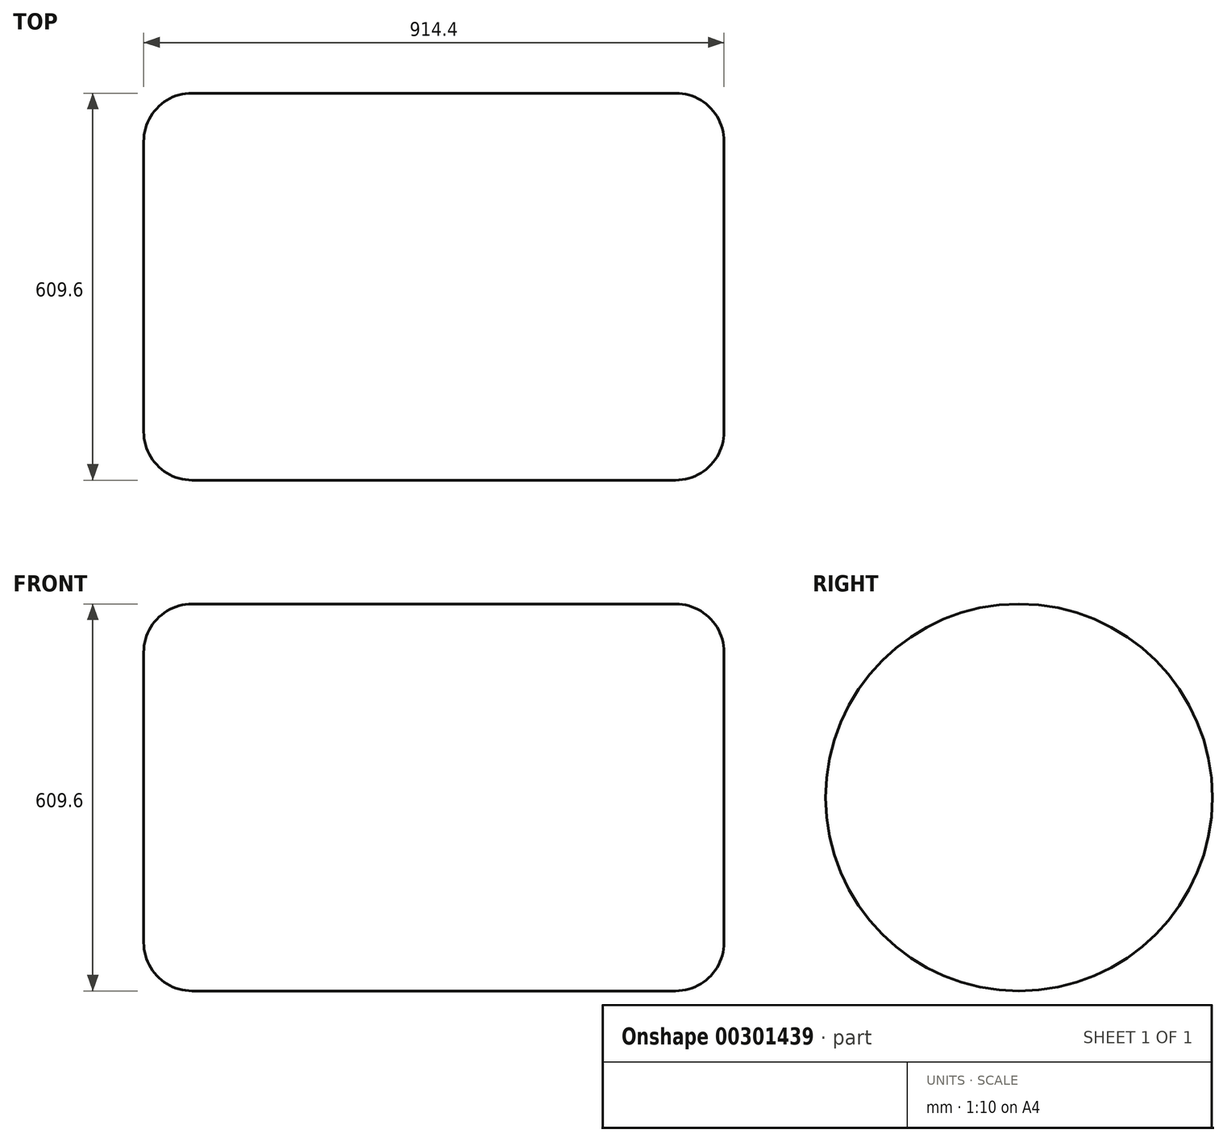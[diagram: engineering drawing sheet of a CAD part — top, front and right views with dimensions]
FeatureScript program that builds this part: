
annotation { "Feature Type Name" : "Feature", "Feature Type Description" : "" }
export const myFeature = defineFeature(function(context is Context, id is Id, definition is map)
    precondition{}
    {
        {
            var Q0;
            Q0=qCreatedBy(makeId("Right.planeOp"),FACE);
            var sketch = newSketch(context, id + "F0", { "sketchPlane" : qUnion([Q0])});
            skCircle(sketch, "E0", {"center": v(0, 0) * mm, "radius": 304.8 * mm});
            skSolve(sketch);
        }
        {
            var Q0;
            Q0=makeQuery(id+"F0.imprint","IMPRINT",FACE,{"disambiguationData":[TD([[makeQuery(id+"F0.imprint","IMPRINT",EDGE,{"derivedFrom":sQuery(id+"F0.wireOp",EDGE,"E0")}),1.0]])]});
            extrude(context, id + "F1", {"entities" : qUnion([Q0]), "depth" : 914.4 * mm});
        }
        {
            var Q0;
            Q0=makeQuery(id+"F1.opExtrude","CAP_EDGE",EDGE,{"disambiguationData":[OSD([sQuery(id+"F0.wireOp",EDGE,"E0")])],"isStart":false});
            var Q1;
            Q1=makeQuery(id+"F1.opExtrude","CAP_EDGE",EDGE,{"disambiguationData":[OSD([sQuery(id+"F0.wireOp",EDGE,"E0")])],"isStart":true});
            fillet(context, id + "F2", {"entities" : qUnion([Q0, Q1]), "radius" : 76.2 * mm, "tangentPropagation" : true, "allowEdgeOverflow" : false});
        }
    });
